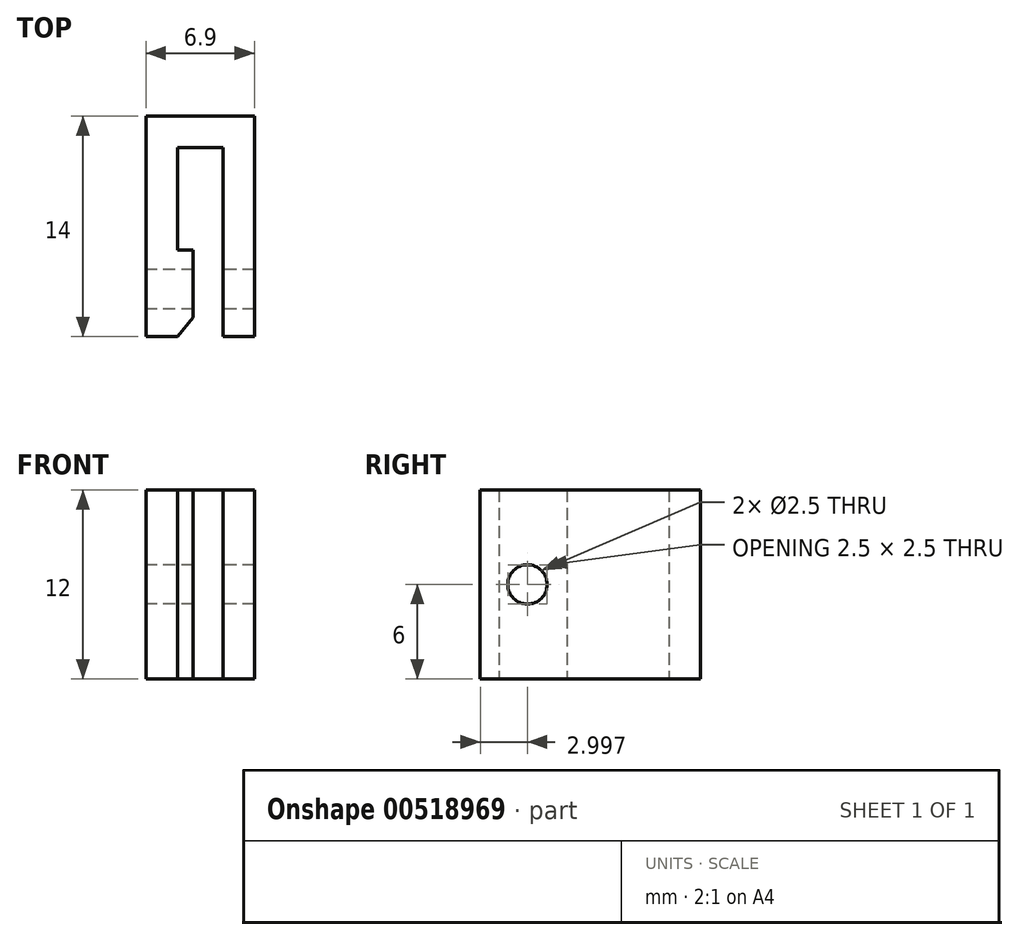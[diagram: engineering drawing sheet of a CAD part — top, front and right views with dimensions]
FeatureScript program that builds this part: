
annotation { "Feature Type Name" : "Feature", "Feature Type Description" : "" }
export const myFeature = defineFeature(function(context is Context, id is Id, definition is map)
    precondition{}
    {
        {
            var Q0;
            Q0=qCreatedBy(makeId("Top.planeOp"),FACE);
            var sketch = newSketch(context, id + "F0", { "sketchPlane" : qUnion([Q0])});
            skLineSegment(sketch, "E0", {"start": v(-6.14, -6.5) * mm, "end": v(-8.14, -6.5) * mm});
            skLineSegment(sketch, "E1", {"start": v(-8.14, -6.5) * mm, "end": v(-8.14, 7.5) * mm});
            skLineSegment(sketch, "E2", {"start": v(-8.14, 7.5) * mm, "end": v(-1.24, 7.5) * mm});
            skLineSegment(sketch, "E3", {"start": v(-1.24, 7.5) * mm, "end": v(-1.24, -6.5) * mm});
            skLineSegment(sketch, "E4", {"start": v(-1.24, -6.5) * mm, "end": v(-3.24, -6.5) * mm});
            skLineSegment(sketch, "E5", {"start": v(-3.24, -6.5) * mm, "end": v(-3.24, 5.5) * mm});
            skLineSegment(sketch, "E6", {"start": v(-3.24, 5.5) * mm, "end": v(-6.14, 5.5) * mm});
            skLineSegment(sketch, "E7", {"start": v(-6.14, 5.5) * mm, "end": v(-6.14, -6.5) * mm});
            skLineSegment(sketch, "E8", {"start": v(-6.14, -1) * mm, "end": v(-5.14, -1) * mm});
            skLineSegment(sketch, "E9", {"start": v(-5.14, -1) * mm, "end": v(-5.14, -5.3) * mm});
            skLineSegment(sketch, "E10", {"start": v(-5.14, -5.3) * mm, "end": v(-6.14, -6.5) * mm});
            skSolve(sketch);
        }
        {
            var Q0;
            Q0=makeQuery(id+"F0.imprint","IMPRINT",FACE,{"disambiguationData":[TD([[makeQuery(id+"F0.imprint","IMPRINT",EDGE,{"derivedFrom":sQuery(id+"F0.wireOp",EDGE,"E0")}),-1.0]])]});
            var Q1;
            {var subQ2=sQuery(id+"F0.wireOp",EDGE,"E8");Q1=makeQuery(id+"F0.imprint","IMPRINT",FACE,{"disambiguationData":[TD([[makeQuery(id+"F0.imprint","IMPRINT",EDGE,{"derivedFrom":subQ2}),-1.0]])]});}
            extrude(context, id + "F1", {"entities" : qUnion([Q0, Q1]), "depth" : 12 * mm, "offsetDistance" : 25 * mm});
        }
        {
            var Q0;
            Q0=makeQuery(id+"F1.opExtrude","SWEPT_FACE",FACE,{"disambiguationData":[OSD([sQuery(id+"F0.wireOp",EDGE,"E1")])]});
            var sketch = newSketch(context, id + "F2", { "sketchPlane" : qUnion([Q0])});
            skCircle(sketch, "E11", {"center": v(3.5, 6) * mm, "radius": 1.25 * mm});
            skPoint(sketch, "E11.centerSnap0", {"position": v(6.5, 6) * mm});
            skCircle(sketch, "E12", {"center": v(3.5, 6) * mm, "radius": 2 * mm});
            skLineSegment(sketch, "E13", {"start": v(3.5, 6) * mm, "end": v(3.5, 12) * mm, "construction": true});
            skLineSegment(sketch, "E14", {"start": v(3.5, 6) * mm, "end": v(3.5, 0) * mm, "construction": true});
            skSolve(sketch);
        }
        {
            var Q0;
            Q0=makeQuery(id+"F2.imprint","IMPRINT",FACE,{"disambiguationData":[TD([[makeQuery(id+"F2.imprint","IMPRINT",EDGE,{"derivedFrom":sQuery(id+"F2.wireOp",EDGE,"E11")}),1.0]])]});
            extrude(context, id + "F3", {"entities" : qUnion([Q0]), "operationType" : NewBodyOperationType.REMOVE, "oppositeDirection" : true, "depth" : 25 * mm, "offsetDistance" : 25 * mm});
        }
    });
